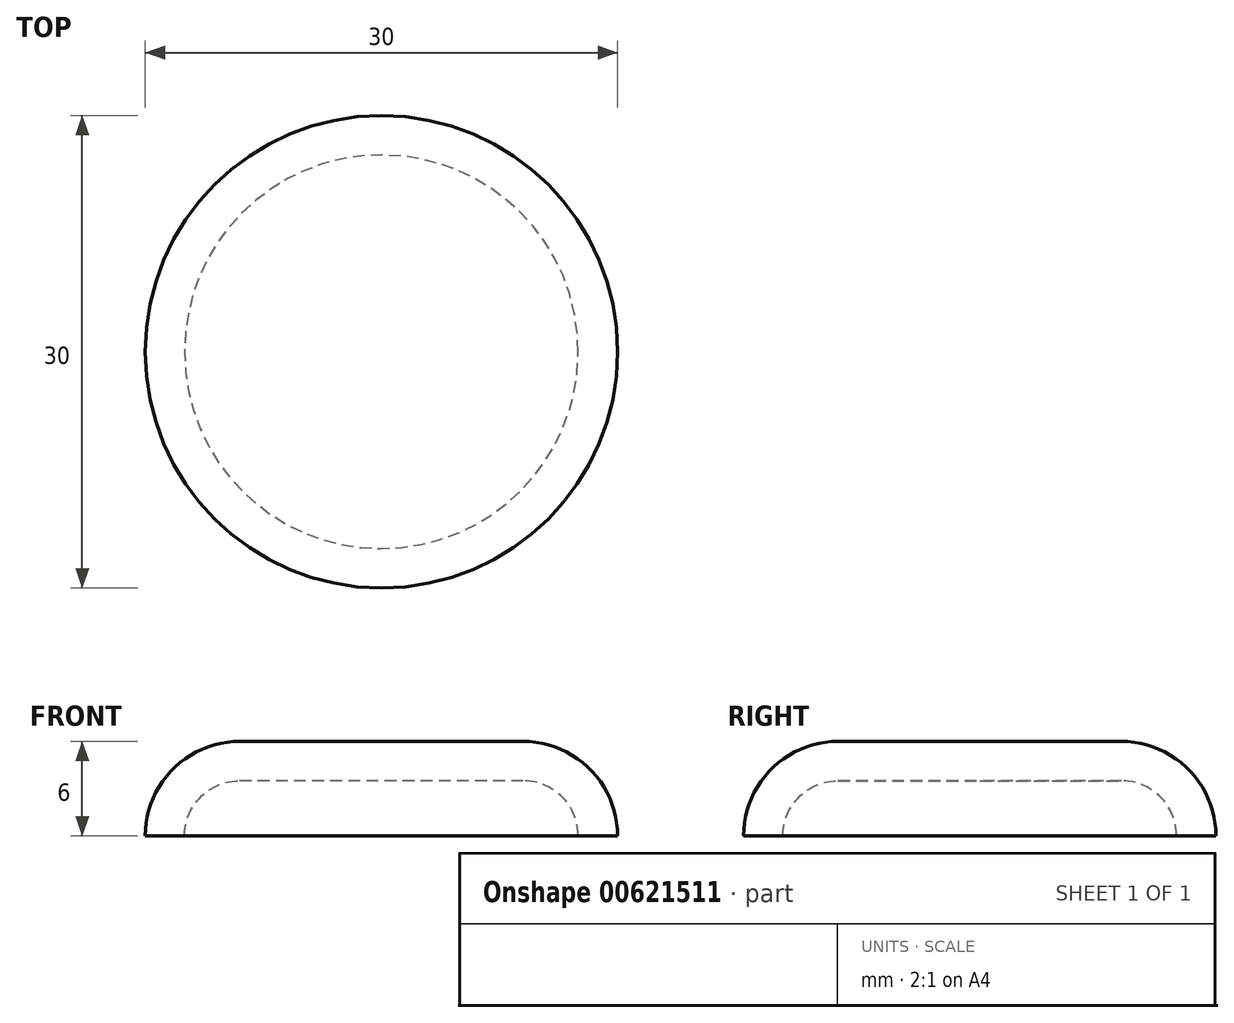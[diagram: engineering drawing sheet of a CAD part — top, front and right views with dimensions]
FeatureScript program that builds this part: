
annotation { "Feature Type Name" : "Feature", "Feature Type Description" : "" }
export const myFeature = defineFeature(function(context is Context, id is Id, definition is map)
    precondition{}
    {
        {
            var Q0;
            Q0=qCreatedBy(makeId("Top.planeOp"),FACE);
            var sketch = newSketch(context, id + "F0", { "sketchPlane" : qUnion([Q0])});
            skCircle(sketch, "E0", {"center": v(0, 0) * mm, "radius": 15 * mm});
            skSolve(sketch);
        }
        {
            var Q0;
            Q0 = qSketchRegion(id + "F0", true);
            extrude(context, id + "F1", {"entities" : qUnion([Q0]), "depth" : 6 * mm, "offsetDistance" : 25 * mm});
        }
        {
            var Q0;
            Q0=makeQuery(id+"F1.opExtrude","CAP_FACE",FACE,{"disambiguationData":[OSD([sQuery(id+"F0.wireOp",EDGE,"E0")])],"isStart":false});
            fillet(context, id + "F2", {"entities" : qUnion([Q0]), "radius" : 6 * mm, "tangentPropagation" : true, "allowEdgeOverflow" : false});
        }
        {
            var Q0;
            Q0=makeQuery(id+"F1.opExtrude","CAP_FACE",FACE,{"disambiguationData":[OSD([sQuery(id+"F0.wireOp",EDGE,"E0")])],"isStart":true});
            shell(context, id + "F3", {"entities" : qUnion([Q0]), "thickness" : 2.5 * mm});
        }
    });
